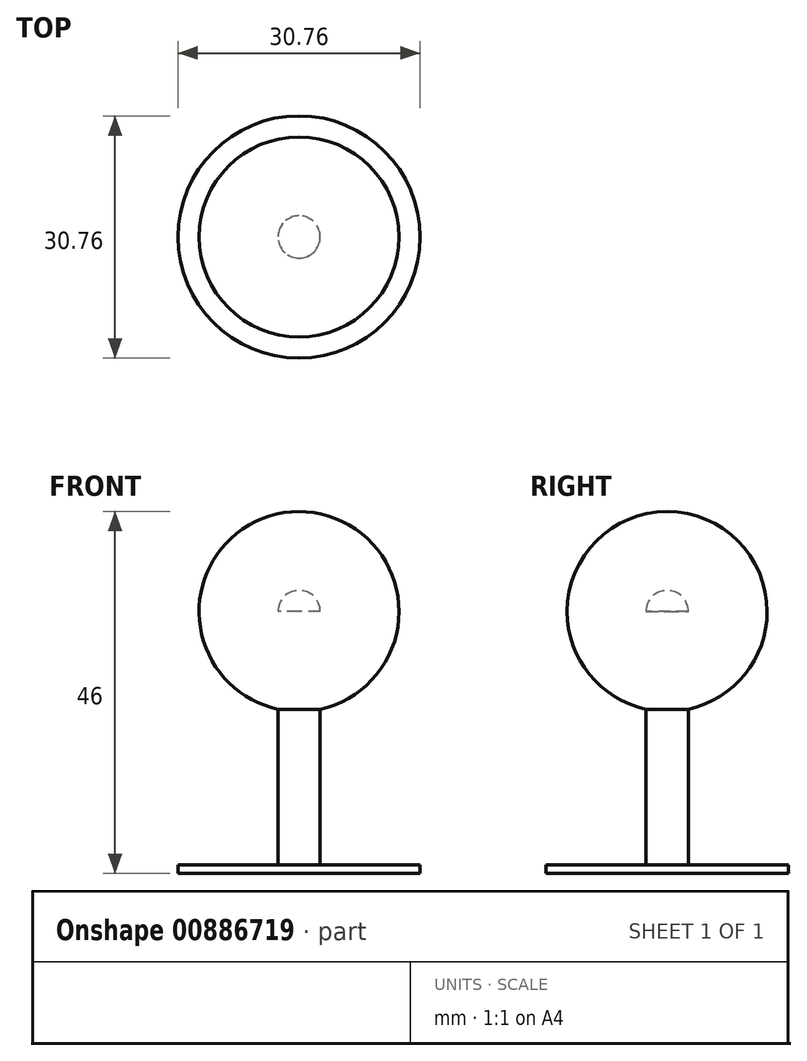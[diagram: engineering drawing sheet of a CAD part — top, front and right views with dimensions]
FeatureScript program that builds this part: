
annotation { "Feature Type Name" : "Feature", "Feature Type Description" : "" }
export const myFeature = defineFeature(function(context is Context, id is Id, definition is map)
    precondition{}
    {
        {
            var Q0;
            Q0=qCreatedBy(makeId("Top.planeOp"),FACE);
            var sketch = newSketch(context, id + "F0", { "sketchPlane" : qUnion([Q0])});
            skCircle(sketch, "E0", {"center": v(0, 0) * mm, "radius": 15.38 * mm});
            skSolve(sketch);
        }
        {
            var Q0;
            Q0 = qSketchRegion(id + "F0", true);
            extrude(context, id + "F1", {"entities" : qUnion([Q0]), "depth" : 1.1 * mm, "offsetDistance" : 25 * mm});
        }
        {
            var Q0;
            Q0=makeQuery(id+"F1.opExtrude","CAP_FACE",FACE,{"disambiguationData":[OSD([sQuery(id+"F0.wireOp",EDGE,"E0")])],"isStart":false});
            var sketch = newSketch(context, id + "F2", { "sketchPlane" : qUnion([Q0])});
            skCircle(sketch, "E1", {"center": v(0, 0) * mm, "radius": 2.69 * mm});
            skSolve(sketch);
        }
        {
            var Q0;
            Q0 = qSketchRegion(id + "F2", true);
            extrude(context, id + "F3", {"entities" : qUnion([Q0]), "operationType" : NewBodyOperationType.ADD, "depth" : 32.2 * mm, "offsetDistance" : 25 * mm});
        }
        {
            var Q0;
            Q0=makeQuery(id+"F3.opExtrude","CAP_FACE",FACE,{"disambiguationData":[OSD([sQuery(id+"F2.wireOp",EDGE,"E1")])],"isStart":false});
            var sketch = newSketch(context, id + "F4", { "sketchPlane" : qUnion([Q0])});
            skCircle(sketch, "E2", {"center": v(0, 0) * mm, "radius": 12.7 * mm});
            skLineSegment(sketch, "E3", {"start": v(0, 12.7) * mm, "end": v(0, -12.7) * mm});
            skSolve(sketch);
        }
        {
            var Q0;
            {var subQ0=sQuery(id+"F4.wireOp",EDGE,"E3");var subQ1=sQuery(id+"F4.wireOp",EDGE,"E2");var subQ2=makeQuery(id+"F4.imprint","INTERSECT",VERTEX,{"disambiguationData":[OD(0.0)],"derivedFrom":[subQ1,subQ0]});Q0=makeQuery(id+"F4.imprint","IMPRINT",FACE,{"disambiguationData":[TD([[makeQuery(id+"F4.imprint","IMPRINT",EDGE,{"disambiguationData":[TD([[subQ2,-1.0]])],"derivedFrom":subQ1}),1.0]])]});}
            var Q1;
            Q1=sQuery(id+"F4.wireOp",EDGE,"E3");
            revolve(context, id + "F5", {"operationType" : NewBodyOperationType.ADD, "surfaceOperationType" : NewSurfaceOperationType.NEW, "entities" : qUnion([Q0]), "axis" : qUnion([Q1]), "revolveType" : RevolveType.FULL});
        }
    });
